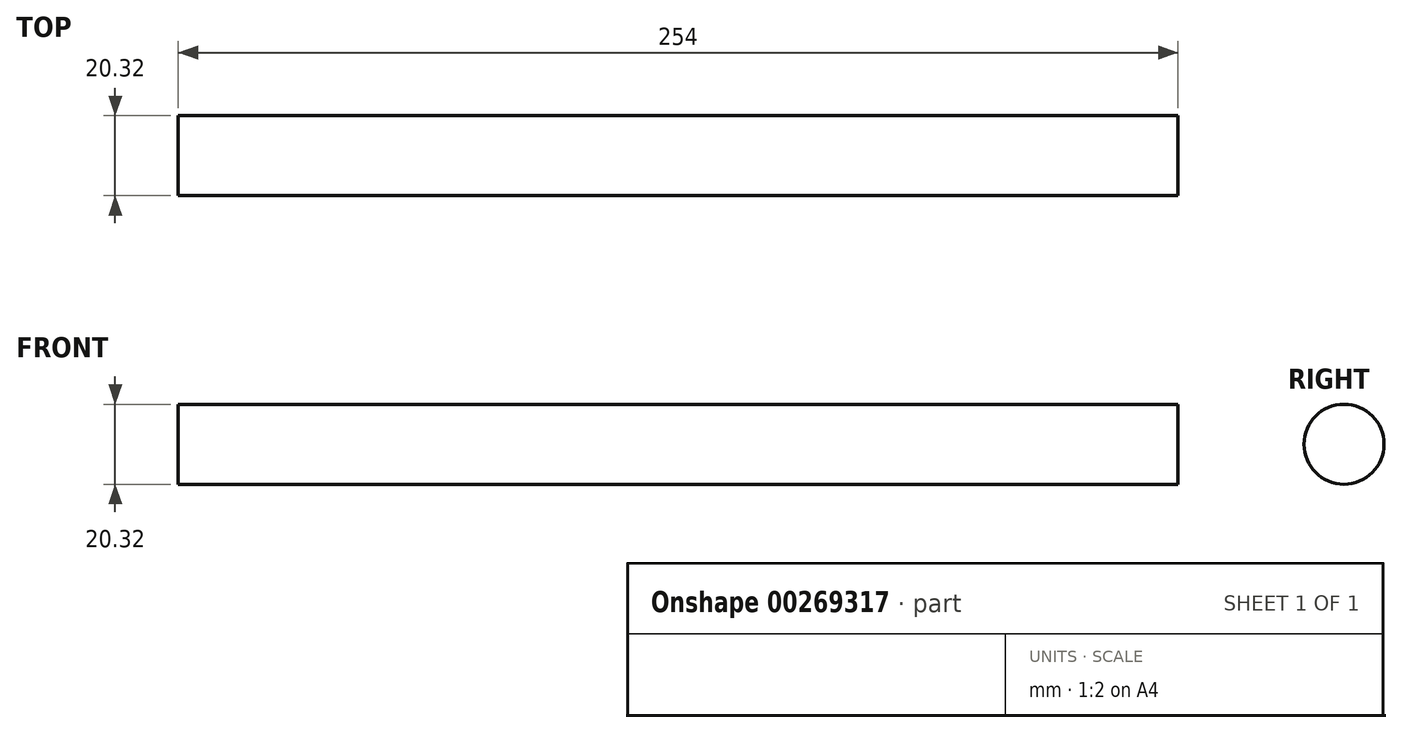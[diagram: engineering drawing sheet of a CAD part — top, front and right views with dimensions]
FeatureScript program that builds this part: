
annotation { "Feature Type Name" : "Feature", "Feature Type Description" : "" }
export const myFeature = defineFeature(function(context is Context, id is Id, definition is map)
    precondition{}
    {
        {
            var Q0;
            Q0=qCreatedBy(makeId("Front.planeOp"),FACE);
            var sketch = newSketch(context, id + "F1", { "sketchPlane" : qUnion([Q0])});
            skLineSegment(sketch, "E0.bottom", {"start": v(0, 0) * mm, "end": v(254, 0) * mm});
            skLineSegment(sketch, "E0.top", {"start": v(0, 10.16) * mm, "end": v(254, 10.16) * mm});
            skLineSegment(sketch, "E0.left", {"start": v(0, 0) * mm, "end": v(0, 10.16) * mm});
            skLineSegment(sketch, "E0.right", {"start": v(254, 0) * mm, "end": v(254, 10.16) * mm});
            skSolve(sketch);
        }
        {
            var Q0;
            Q0=makeQuery(id+"F1.imprint","IMPRINT",FACE,{"disambiguationData":[TD([[makeQuery(id+"F1.imprint","IMPRINT",EDGE,{"derivedFrom":sQuery(id+"F1.wireOp",EDGE,"E0.bottom")}),1.0]])]});
            var Q1;
            Q1=sQuery(id+"F1.wireOp",EDGE,"E0.bottom");
            revolve(context, id + "F0", {"entities" : qUnion([Q0]), "axis" : qUnion([Q1]), "revolveType" : RevolveType.FULL});
        }
    });
